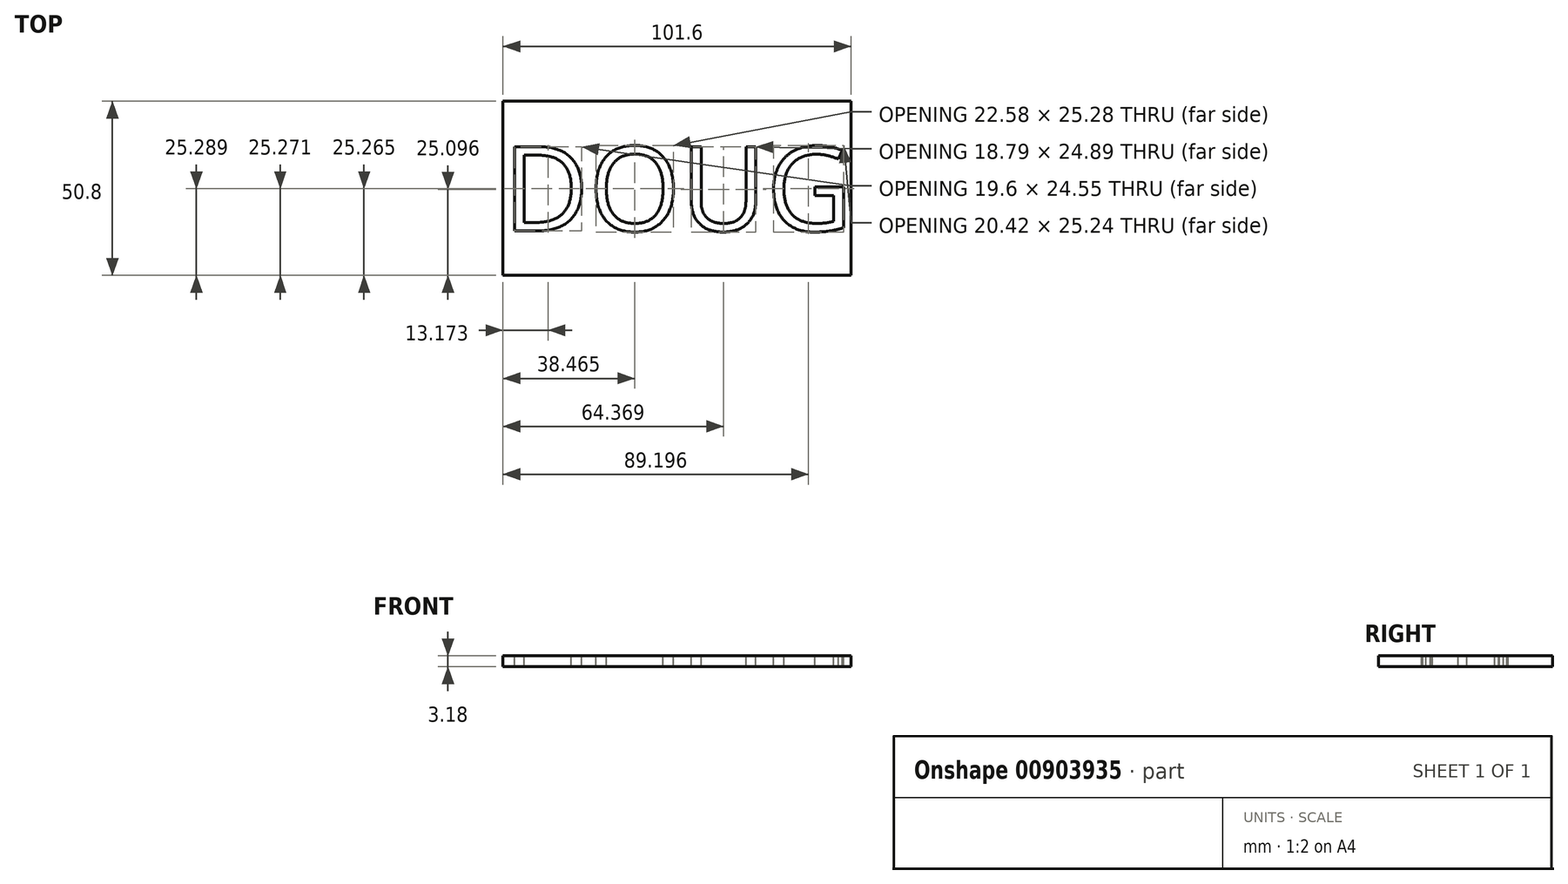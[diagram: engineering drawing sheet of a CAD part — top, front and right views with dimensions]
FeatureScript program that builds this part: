
annotation { "Feature Type Name" : "Feature", "Feature Type Description" : "" }
export const myFeature = defineFeature(function(context is Context, id is Id, definition is map)
    precondition{}
    {
        {
            var Q0;
            Q0=qCreatedBy(makeId("Top.planeOp"),FACE);
            var sketch = newSketch(context, id + "F0", { "sketchPlane" : qUnion([Q0])});
            skLineSegment(sketch, "E0.bottom", {"start": v(0, 0) * mm, "end": v(101.6, 0) * mm});
            skLineSegment(sketch, "E0.top", {"start": v(0, 50.8) * mm, "end": v(101.6, 50.8) * mm});
            skLineSegment(sketch, "E0.left", {"start": v(0, 0) * mm, "end": v(0, 50.8) * mm});
            skLineSegment(sketch, "E0.right", {"start": v(101.6, 0) * mm, "end": v(101.6, 50.8) * mm});
            skSolve(sketch);
        }
        {
            var Q0;
            Q0 = qSketchRegion(id + "F0", true);
            extrude(context, id + "F1", {"entities" : qUnion([Q0]), "depth" : 3.17 * mm, "offsetDistance" : 25.4 * mm});
        }
        {
            var Q0;
            Q0=makeQuery(id+"F1.opExtrude","CAP_FACE",FACE,{"disambiguationData":[OSD([sQuery(id+"F0.wireOp",EDGE,"E0.bottom"),sQuery(id+"F0.wireOp",EDGE,"E0.top"),sQuery(id+"F0.wireOp",EDGE,"E0.left"),sQuery(id+"F0.wireOp",EDGE,"E0.right")])],"isStart":false});
            var sketch = newSketch(context, id + "F2", { "sketchPlane" : qUnion([Q0])});
            skText(sketch, "E1", { "text": "DOUG", "fontName": "OpenSans-Regular.ttf"});
            const initialGuessF2  = {"E1": [0, 0.01299, 1, 0, 0.02476]};
            skSetInitialGuess(sketch, initialGuessF2);
            skSolve(sketch);
        }
        {
            var Q0;
            Q0 = qSketchRegion(id + "F2", true);
            extrude(context, id + "F3", {"entities" : qUnion([Q0]), "operationType" : NewBodyOperationType.REMOVE, "oppositeDirection" : true, "depth" : 25.4 * mm, "offsetDistance" : 25.4 * mm});
        }
    });
